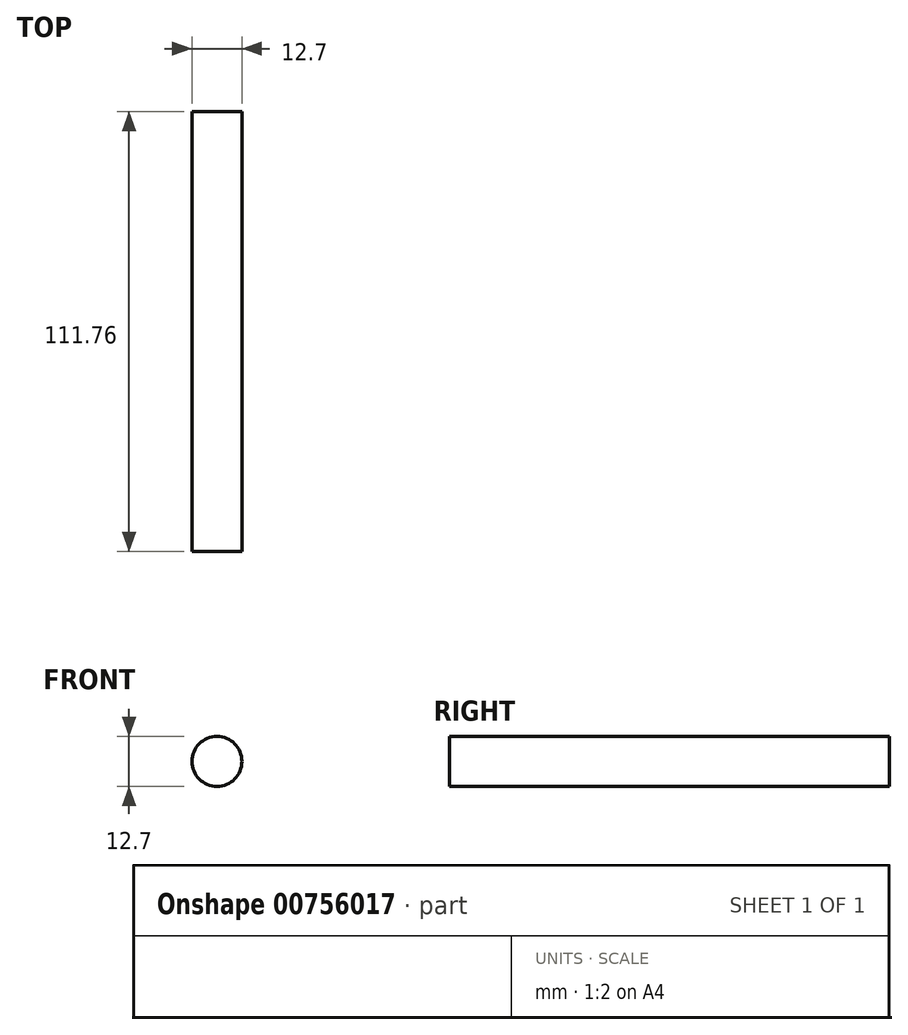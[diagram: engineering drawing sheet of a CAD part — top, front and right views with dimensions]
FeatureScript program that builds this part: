
annotation { "Feature Type Name" : "Feature", "Feature Type Description" : "" }
export const myFeature = defineFeature(function(context is Context, id is Id, definition is map)
    precondition{}
    {
        {
            var Q0;
            Q0=qCreatedBy(makeId("Front.planeOp"),FACE);
            var sketch = newSketch(context, id + "F0", { "sketchPlane" : qUnion([Q0])});
            skCircle(sketch, "E0", {"center": v(0.8, 0.96) * mm, "radius": 6.35 * mm});
            skSolve(sketch);
        }
        {
            var Q0;
            Q0=makeQuery(id+"F0.imprint","IMPRINT",FACE,{"disambiguationData":[TD([[makeQuery(id+"F0.imprint","IMPRINT",EDGE,{"derivedFrom":sQuery(id+"F0.wireOp",EDGE,"E0")}),1.0]])]});
            extrude(context, id + "F1", {"entities" : qUnion([Q0]), "depth" : 111.76 * mm, "offsetDistance" : 25.4 * mm});
        }
    });
